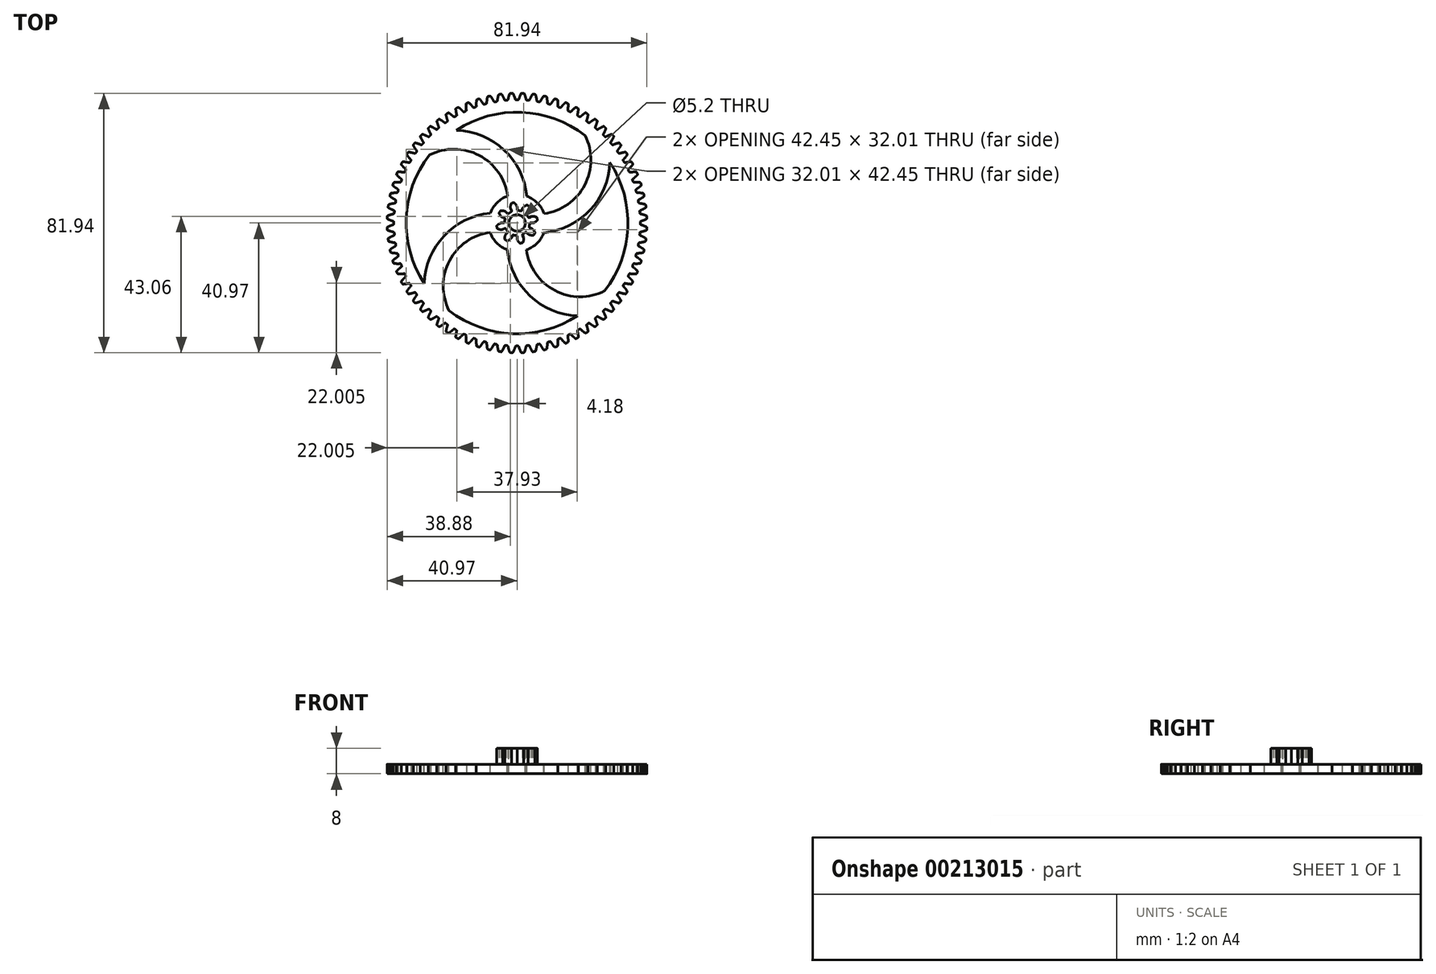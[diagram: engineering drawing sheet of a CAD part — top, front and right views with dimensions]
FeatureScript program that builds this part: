
annotation { "Feature Type Name" : "Feature", "Feature Type Description" : "" }
export const myFeature = defineFeature(function(context is Context, id is Id, definition is map)
    precondition{}
    {
        {
            var Q0;
            Q0=qCreatedBy(makeId("Top.planeOp"),FACE);
            var sketch = newSketch(context, id + "F0", { "sketchPlane" : qUnion([Q0])});
            skCircle(sketch, "E0", {"center": v(0, 0) * mm, "radius": 37.59 * mm, "construction": true});
            skLineSegment(sketch, "E1", {"start": v(37.59, 0) * mm, "end": v(37.59, 0) * mm});
            skLineSegment(sketch, "E2", {"start": v(0, 0) * mm, "end": v(37.55, 1.64) * mm, "construction": true});
            skLineSegment(sketch, "E3", {"start": v(37.55, 1.64) * mm, "end": v(37.62, 0) * mm, "construction": true});
            skLineSegment(sketch, "E4", {"start": v(0, 0) * mm, "end": v(37.44, 3.28) * mm, "construction": true});
            skLineSegment(sketch, "E5", {"start": v(37.44, 3.28) * mm, "end": v(37.73, 0) * mm, "construction": true});
            skLineSegment(sketch, "E6", {"start": v(0, 0) * mm, "end": v(37.27, 4.9) * mm, "construction": true});
            skLineSegment(sketch, "E7", {"start": v(37.27, 4.9) * mm, "end": v(37.9, 0.03) * mm, "construction": true});
            skLineSegment(sketch, "E8", {"start": v(0, 0) * mm, "end": v(37.02, 6.53) * mm, "construction": true});
            skLineSegment(sketch, "E9", {"start": v(37.02, 6.53) * mm, "end": v(38.16, 0.07) * mm, "construction": true});
            skLineSegment(sketch, "E10", {"start": v(0, 0) * mm, "end": v(36.7, 8.14) * mm, "construction": true});
            skLineSegment(sketch, "E11", {"start": v(36.7, 8.14) * mm, "end": v(38.47, 0.13) * mm, "construction": true});
            skLineSegment(sketch, "E12", {"start": v(0, 0) * mm, "end": v(36.3, 9.73) * mm, "construction": true});
            skLineSegment(sketch, "E13", {"start": v(36.3, 9.73) * mm, "end": v(38.85, 0.22) * mm, "construction": true});
            skLineSegment(sketch, "E14", {"start": v(0, 0) * mm, "end": v(35.85, 11.3) * mm, "construction": true});
            skLineSegment(sketch, "E15", {"start": v(35.85, 11.3) * mm, "end": v(39.3, 0.35) * mm, "construction": true});
            skLineSegment(sketch, "E16", {"start": v(0, 0) * mm, "end": v(35.32, 12.86) * mm, "construction": true});
            skLineSegment(sketch, "E17", {"start": v(35.32, 12.86) * mm, "end": v(39.8, 0.53) * mm, "construction": true});
            skLineSegment(sketch, "E18", {"start": v(0, 0) * mm, "end": v(34.73, 14.38) * mm, "construction": true});
            skLineSegment(sketch, "E19", {"start": v(34.73, 14.38) * mm, "end": v(40.38, 0.75) * mm, "construction": true});
            skLineSegment(sketch, "E20", {"start": v(0, 0) * mm, "end": v(34.07, 15.89) * mm, "construction": true});
            skLineSegment(sketch, "E21", {"start": v(34.07, 15.89) * mm, "end": v(41, 1.02) * mm, "construction": true});
            skPoint(sketch, "E22", {"position": v(37.59, 0) * mm});
            skCircle(sketch, "E23", {"center": v(0, 0) * mm, "radius": 38.89 * mm});
            skFitSpline(sketch, "E24", {"points": [v(37.59, 0) * mm, v(37.62, 0) * mm, v(37.73, 0) * mm, v(37.9, 0.03) * mm, v(38.16, 0.07) * mm, v(38.47, 0.13) * mm, v(38.85, 0.22) * mm, v(39.3, 0.35) * mm, v(39.8, 0.53) * mm, v(40.38, 0.75) * mm, v(41, 1.02) * mm], "startDerivative": vector(0.94, 0.02) * mm, "endDerivative": vector(4.3, 1.94) * mm, "construction": true});
            skPoint(sketch, "E25", {"position": v(40.99, 1.02) * mm});
            skPoint(sketch, "E26", {"position": v(38.89, 0.23) * mm});
            skFitSpline(sketch, "E27", {"points": [v(37.59, 0) * mm, v(37.62, 0) * mm, v(37.73, 0) * mm, v(37.9, 0.03) * mm, v(38.16, 0.07) * mm, v(38.47, 0.13) * mm, v(38.85, 0.22) * mm, v(39.3, 0.35) * mm, v(39.8, 0.53) * mm, v(40.38, 0.75) * mm, v(41, 1.02) * mm], "startDerivative": vector(0.94, 0.02) * mm, "endDerivative": vector(4.3, 1.94) * mm});
            skLineSegment(sketch, "E28", {"start": v(0, 0) * mm, "end": v(51.23, 1.88) * mm, "construction": true});
            skFitSpline(sketch, "E29.MirrorCS", {"points": [v(37.49, 2.76) * mm, v(37.52, 2.76) * mm, v(37.63, 2.76) * mm, v(37.8, 2.75) * mm, v(38.06, 2.73) * mm, v(38.38, 2.7) * mm, v(38.77, 2.63) * mm, v(39.22, 2.53) * mm, v(39.74, 2.4) * mm, v(40.32, 2.22) * mm, v(40.96, 1.99) * mm], "startDerivative": vector(0.93, 0.05) * mm, "endDerivative": vector(4.43, -1.62) * mm});
            skArc(sketch, "E30", {"start": v(40.95, 2) * mm, "mid": v(-40.97, -1.5) * mm, "end": v(40.99, 1.02) * mm, "construction": true});
            skArc(sketch, "E31", {"start": v(40.99, 1.02) * mm, "mid": v(40.97, 1.5) * mm, "end": v(40.95, 2) * mm});
            skSolve(sketch);
        }
        {
            var Q0;
            Q0=qCreatedBy(makeId("Front.planeOp"),FACE);
            var sketch = newSketch(context, id + "F1", { "sketchPlane" : qUnion([Q0])});
            skLineSegment(sketch, "E32", {"start": v(0, 0) * mm, "end": v(0, 57.42) * mm, "construction": true});
            skSolve(sketch);
        }
        {
            var Q0;
            {var subQ0=sQuery(id+"F0.wireOp",EDGE,"E23");var subQ1=makeQuery(id+"F0.imprint","INTERSECT",VERTEX,{"derivedFrom":[subQ0,sQuery(id+"F0.wireOp",EDGE,"E27")]});Q0=makeQuery(id+"F0.imprint","IMPRINT",FACE,{"disambiguationData":[TD([[makeQuery(id+"F0.imprint","IMPRINT",EDGE,{"disambiguationData":[TD([[subQ1,-1.0]])],"derivedFrom":subQ0}),1.0]])]});}
            var Q1;
            {var subQ0=sQuery(id+"F0.wireOp",EDGE,"E27");Q1=makeQuery(id+"F0.imprint","IMPRINT",FACE,{"disambiguationData":[TD([[makeQuery(id+"F0.imprint","IMPRINT",EDGE,{"derivedFrom":subQ0}),1.0]])]});}
            extrude(context, id + "F2", {"entities" : qUnion([Q0, Q1]), "depth" : 3 * mm});
        }
        {
            var Q0;
            Q0=makeQuery(id+"F2.opExtrude","SWEPT_EDGE",EDGE,{"disambiguationData":[OSD([sQuery(id+"F0.wireOp",EDGE,"E23"),sQuery(id+"F0.wireOp",EDGE,"E29.MirrorCS")])]});
            var Q1;
            Q1=makeQuery(id+"F2.opExtrude","SWEPT_EDGE",EDGE,{"disambiguationData":[OSD([sQuery(id+"F0.wireOp",EDGE,"E29.MirrorCS"),sQuery(id+"F0.wireOp",EDGE,"E31")])]});
            var Q2;
            Q2=makeQuery(id+"F2.opExtrude","SWEPT_EDGE",EDGE,{"disambiguationData":[OSD([sQuery(id+"F0.wireOp",EDGE,"E27"),sQuery(id+"F0.wireOp",EDGE,"E31")])]});
            var Q3;
            Q3=makeQuery(id+"F2.opExtrude","SWEPT_EDGE",EDGE,{"disambiguationData":[OSD([sQuery(id+"F0.wireOp",EDGE,"E23"),sQuery(id+"F0.wireOp",EDGE,"E27")])]});
            fillet(context, id + "F3", {"entities" : qUnion([Q0, Q1, Q2, Q3]), "radius" : 0.3 * mm, "tangentPropagation" : true, "allowEdgeOverflow" : false});
        }
        {
            var Q0;
            Q0=makeQuery(id+"F2.opExtrude","SWEPT_BODY",BODY,{"disambiguationData":[OSD([sQuery(id+"F0.wireOp",EDGE,"E23"),sQuery(id+"F0.wireOp",EDGE,"E27"),sQuery(id+"F0.wireOp",EDGE,"E29.MirrorCS"),sQuery(id+"F0.wireOp",EDGE,"E31")])]});
            var Q1;
            Q1=sQuery(id+"F1.wireOp",EDGE,"E32");
            circularPattern(context, id + "F4", {"operationType" : NewBodyOperationType.ADD, "entities" : qUnion([Q0]), "axis" : qUnion([Q1]), "angle" : 360 * degree, "instanceCount" : 72, "equalSpace" : true});
        }
        {
            var Q0;
            {var subQ0=makeQuery(id+"F2.opExtrude","CAP_FACE",FACE,{"disambiguationData":[OSD([sQuery(id+"F0.wireOp",EDGE,"E23"),sQuery(id+"F0.wireOp",EDGE,"E27"),sQuery(id+"F0.wireOp",EDGE,"E29.MirrorCS"),sQuery(id+"F0.wireOp",EDGE,"E31")])],"isStart":false});Q0=makeQuery(id+"F4.boolean.opBoolean","MERGE",FACE,{"derivedFrom":[subQ0,makeQuery(id+"F4.opPattern","COPY",FACE,{"derivedFrom":subQ0,"instanceName":"1"}),makeQuery(id+"F4.opPattern","COPY",FACE,{"derivedFrom":subQ0,"instanceName":"2"}),makeQuery(id+"F4.opPattern","COPY",FACE,{"derivedFrom":subQ0,"instanceName":"3"}),makeQuery(id+"F4.opPattern","COPY",FACE,{"derivedFrom":subQ0,"instanceName":"4"}),makeQuery(id+"F4.opPattern","COPY",FACE,{"derivedFrom":subQ0,"instanceName":"5"}),makeQuery(id+"F4.opPattern","COPY",FACE,{"derivedFrom":subQ0,"instanceName":"6"}),makeQuery(id+"F4.opPattern","COPY",FACE,{"derivedFrom":subQ0,"instanceName":"7"}),makeQuery(id+"F4.opPattern","COPY",FACE,{"derivedFrom":subQ0,"instanceName":"8"}),makeQuery(id+"F4.opPattern","COPY",FACE,{"derivedFrom":subQ0,"instanceName":"9"}),makeQuery(id+"F4.opPattern","COPY",FACE,{"derivedFrom":subQ0,"instanceName":"10"}),makeQuery(id+"F4.opPattern","COPY",FACE,{"derivedFrom":subQ0,"instanceName":"11"}),makeQuery(id+"F4.opPattern","COPY",FACE,{"derivedFrom":subQ0,"instanceName":"12"}),makeQuery(id+"F4.opPattern","COPY",FACE,{"derivedFrom":subQ0,"instanceName":"13"}),makeQuery(id+"F4.opPattern","COPY",FACE,{"derivedFrom":subQ0,"instanceName":"14"}),makeQuery(id+"F4.opPattern","COPY",FACE,{"derivedFrom":subQ0,"instanceName":"15"}),makeQuery(id+"F4.opPattern","COPY",FACE,{"derivedFrom":subQ0,"instanceName":"16"}),makeQuery(id+"F4.opPattern","COPY",FACE,{"derivedFrom":subQ0,"instanceName":"17"}),makeQuery(id+"F4.opPattern","COPY",FACE,{"derivedFrom":subQ0,"instanceName":"18"}),makeQuery(id+"F4.opPattern","COPY",FACE,{"derivedFrom":subQ0,"instanceName":"19"}),makeQuery(id+"F4.opPattern","COPY",FACE,{"derivedFrom":subQ0,"instanceName":"20"}),makeQuery(id+"F4.opPattern","COPY",FACE,{"derivedFrom":subQ0,"instanceName":"21"}),makeQuery(id+"F4.opPattern","COPY",FACE,{"derivedFrom":subQ0,"instanceName":"22"}),makeQuery(id+"F4.opPattern","COPY",FACE,{"derivedFrom":subQ0,"instanceName":"23"}),makeQuery(id+"F4.opPattern","COPY",FACE,{"derivedFrom":subQ0,"instanceName":"24"}),makeQuery(id+"F4.opPattern","COPY",FACE,{"derivedFrom":subQ0,"instanceName":"25"}),makeQuery(id+"F4.opPattern","COPY",FACE,{"derivedFrom":subQ0,"instanceName":"26"}),makeQuery(id+"F4.opPattern","COPY",FACE,{"derivedFrom":subQ0,"instanceName":"27"}),makeQuery(id+"F4.opPattern","COPY",FACE,{"derivedFrom":subQ0,"instanceName":"28"}),makeQuery(id+"F4.opPattern","COPY",FACE,{"derivedFrom":subQ0,"instanceName":"29"}),makeQuery(id+"F4.opPattern","COPY",FACE,{"derivedFrom":subQ0,"instanceName":"30"}),makeQuery(id+"F4.opPattern","COPY",FACE,{"derivedFrom":subQ0,"instanceName":"31"}),makeQuery(id+"F4.opPattern","COPY",FACE,{"derivedFrom":subQ0,"instanceName":"32"}),makeQuery(id+"F4.opPattern","COPY",FACE,{"derivedFrom":subQ0,"instanceName":"33"}),makeQuery(id+"F4.opPattern","COPY",FACE,{"derivedFrom":subQ0,"instanceName":"34"}),makeQuery(id+"F4.opPattern","COPY",FACE,{"derivedFrom":subQ0,"instanceName":"35"}),makeQuery(id+"F4.opPattern","COPY",FACE,{"derivedFrom":subQ0,"instanceName":"36"}),makeQuery(id+"F4.opPattern","COPY",FACE,{"derivedFrom":subQ0,"instanceName":"37"}),makeQuery(id+"F4.opPattern","COPY",FACE,{"derivedFrom":subQ0,"instanceName":"38"}),makeQuery(id+"F4.opPattern","COPY",FACE,{"derivedFrom":subQ0,"instanceName":"39"}),makeQuery(id+"F4.opPattern","COPY",FACE,{"derivedFrom":subQ0,"instanceName":"40"}),makeQuery(id+"F4.opPattern","COPY",FACE,{"derivedFrom":subQ0,"instanceName":"41"}),makeQuery(id+"F4.opPattern","COPY",FACE,{"derivedFrom":subQ0,"instanceName":"42"}),makeQuery(id+"F4.opPattern","COPY",FACE,{"derivedFrom":subQ0,"instanceName":"43"}),makeQuery(id+"F4.opPattern","COPY",FACE,{"derivedFrom":subQ0,"instanceName":"44"}),makeQuery(id+"F4.opPattern","COPY",FACE,{"derivedFrom":subQ0,"instanceName":"45"}),makeQuery(id+"F4.opPattern","COPY",FACE,{"derivedFrom":subQ0,"instanceName":"46"}),makeQuery(id+"F4.opPattern","COPY",FACE,{"derivedFrom":subQ0,"instanceName":"47"}),makeQuery(id+"F4.opPattern","COPY",FACE,{"derivedFrom":subQ0,"instanceName":"48"}),makeQuery(id+"F4.opPattern","COPY",FACE,{"derivedFrom":subQ0,"instanceName":"49"}),makeQuery(id+"F4.opPattern","COPY",FACE,{"derivedFrom":subQ0,"instanceName":"50"}),makeQuery(id+"F4.opPattern","COPY",FACE,{"derivedFrom":subQ0,"instanceName":"51"}),makeQuery(id+"F4.opPattern","COPY",FACE,{"derivedFrom":subQ0,"instanceName":"52"}),makeQuery(id+"F4.opPattern","COPY",FACE,{"derivedFrom":subQ0,"instanceName":"53"}),makeQuery(id+"F4.opPattern","COPY",FACE,{"derivedFrom":subQ0,"instanceName":"54"}),makeQuery(id+"F4.opPattern","COPY",FACE,{"derivedFrom":subQ0,"instanceName":"55"}),makeQuery(id+"F4.opPattern","COPY",FACE,{"derivedFrom":subQ0,"instanceName":"56"}),makeQuery(id+"F4.opPattern","COPY",FACE,{"derivedFrom":subQ0,"instanceName":"57"}),makeQuery(id+"F4.opPattern","COPY",FACE,{"derivedFrom":subQ0,"instanceName":"58"}),makeQuery(id+"F4.opPattern","COPY",FACE,{"derivedFrom":subQ0,"instanceName":"59"}),makeQuery(id+"F4.opPattern","COPY",FACE,{"derivedFrom":subQ0,"instanceName":"60"}),makeQuery(id+"F4.opPattern","COPY",FACE,{"derivedFrom":subQ0,"instanceName":"61"}),makeQuery(id+"F4.opPattern","COPY",FACE,{"derivedFrom":subQ0,"instanceName":"62"}),makeQuery(id+"F4.opPattern","COPY",FACE,{"derivedFrom":subQ0,"instanceName":"63"}),makeQuery(id+"F4.opPattern","COPY",FACE,{"derivedFrom":subQ0,"instanceName":"64"}),makeQuery(id+"F4.opPattern","COPY",FACE,{"derivedFrom":subQ0,"instanceName":"65"}),makeQuery(id+"F4.opPattern","COPY",FACE,{"derivedFrom":subQ0,"instanceName":"66"}),makeQuery(id+"F4.opPattern","COPY",FACE,{"derivedFrom":subQ0,"instanceName":"67"}),makeQuery(id+"F4.opPattern","COPY",FACE,{"derivedFrom":subQ0,"instanceName":"68"}),makeQuery(id+"F4.opPattern","COPY",FACE,{"derivedFrom":subQ0,"instanceName":"69"}),makeQuery(id+"F4.opPattern","COPY",FACE,{"derivedFrom":subQ0,"instanceName":"70"}),makeQuery(id+"F4.opPattern","COPY",FACE,{"derivedFrom":subQ0,"instanceName":"71"})]});}
            var sketch = newSketch(context, id + "F5", { "sketchPlane" : qUnion([Q0])});
            skLineSegment(sketch, "E33", {"start": v(38.93, -0.27) * mm, "end": v(0, 0) * mm, "construction": true});
            skPoint(sketch, "E33.startSnap0", {"position": v(38.89, -0.27) * mm});
            skCircle(sketch, "E34", {"center": v(0, 0) * mm, "radius": 4.97 * mm, "construction": true});
            skLineSegment(sketch, "E35", {"start": v(-2.75, -4.33) * mm, "end": v(-2.75, -4.33) * mm});
            skLineSegment(sketch, "E36", {"start": v(0, 0) * mm, "end": v(4.96, 0.42) * mm, "construction": true});
            skLineSegment(sketch, "E37", {"start": v(4.96, 0.42) * mm, "end": v(5, 0) * mm, "construction": true});
            skLineSegment(sketch, "E38", {"start": v(0, 0) * mm, "end": v(4.9, 0.85) * mm, "construction": true});
            skLineSegment(sketch, "E39", {"start": v(4.9, 0.85) * mm, "end": v(5.05, 0) * mm, "construction": true});
            skLineSegment(sketch, "E40", {"start": v(0, 0) * mm, "end": v(4.81, 1.26) * mm, "construction": true});
            skLineSegment(sketch, "E41", {"start": v(4.81, 1.26) * mm, "end": v(5.14, 0.03) * mm, "construction": true});
            skLineSegment(sketch, "E42", {"start": v(0, 0) * mm, "end": v(4.69, 1.67) * mm, "construction": true});
            skLineSegment(sketch, "E43", {"start": v(4.69, 1.67) * mm, "end": v(5.26, 0.07) * mm, "construction": true});
            skLineSegment(sketch, "E44", {"start": v(0, 0) * mm, "end": v(4.53, 2.06) * mm, "construction": true});
            skLineSegment(sketch, "E45", {"start": v(4.53, 2.06) * mm, "end": v(5.4, 0.13) * mm, "construction": true});
            skLineSegment(sketch, "E46", {"start": v(0, 0) * mm, "end": v(4.33, 2.44) * mm, "construction": true});
            skLineSegment(sketch, "E47", {"start": v(4.33, 2.44) * mm, "end": v(5.59, 0.22) * mm, "construction": true});
            skLineSegment(sketch, "E48", {"start": v(0, 0) * mm, "end": v(4.1, 2.8) * mm, "construction": true});
            skLineSegment(sketch, "E49", {"start": v(4.1, 2.8) * mm, "end": v(5.79, 0.34) * mm, "construction": true});
            skLineSegment(sketch, "E50", {"start": v(0, 0) * mm, "end": v(3.86, 3.14) * mm, "construction": true});
            skLineSegment(sketch, "E51", {"start": v(3.86, 3.14) * mm, "end": v(6, 0.5) * mm, "construction": true});
            skLineSegment(sketch, "E52", {"start": v(0, 0) * mm, "end": v(3.57, 3.46) * mm, "construction": true});
            skLineSegment(sketch, "E53", {"start": v(3.57, 3.46) * mm, "end": v(6.24, 0.71) * mm, "construction": true});
            skLineSegment(sketch, "E54", {"start": v(0, 0) * mm, "end": v(3.26, 3.75) * mm, "construction": true});
            skLineSegment(sketch, "E55", {"start": v(3.26, 3.75) * mm, "end": v(6.47, 0.96) * mm, "construction": true});
            skPoint(sketch, "E56", {"position": v(4.97, 0) * mm});
            skCircle(sketch, "E57", {"center": v(0, 0) * mm, "radius": 3.97 * mm});
            skLineSegment(sketch, "E58", {"start": v(3.97, 0) * mm, "end": v(4.97, 0) * mm});
            skFitSpline(sketch, "E59", {"points": [v(4.97, 0) * mm, v(5, 0) * mm, v(5.05, 0) * mm, v(5.14, 0.03) * mm, v(5.26, 0.07) * mm, v(5.4, 0.13) * mm, v(5.59, 0.22) * mm, v(5.79, 0.34) * mm, v(6, 0.5) * mm, v(6.24, 0.71) * mm, v(6.47, 0.96) * mm], "startDerivative": vector(0.48, 0.02) * mm, "endDerivative": vector(1.62, 1.77) * mm});
            skFitSpline(sketch, "E60", {"points": [v(4.97, 0) * mm, v(5, 0) * mm, v(5.05, 0) * mm, v(5.14, 0.03) * mm, v(5.26, 0.07) * mm, v(5.4, 0.13) * mm, v(5.59, 0.22) * mm, v(5.79, 0.34) * mm, v(6, 0.5) * mm, v(6.24, 0.71) * mm, v(6.47, 0.96) * mm], "startDerivative": vector(0.48, 0.02) * mm, "endDerivative": vector(1.62, 1.77) * mm, "construction": true});
            skLineSegment(sketch, "E61", {"start": v(0, 0) * mm, "end": v(9.9, 2.12) * mm, "construction": true});
            skLineSegment(sketch, "E62.MirrorCS", {"start": v(3.62, 1.63) * mm, "end": v(4.54, 2.04) * mm});
            skFitSpline(sketch, "E63.MirrorCS", {"points": [v(4.54, 2.04) * mm, v(4.55, 2.05) * mm, v(4.6, 2.06) * mm, v(4.7, 2.08) * mm, v(4.82, 2.1) * mm, v(4.99, 2.1) * mm, v(5.19, 2.1) * mm, v(5.42, 2.06) * mm, v(5.69, 2) * mm, v(5.98, 1.9) * mm, v(6.3, 1.78) * mm], "startDerivative": vector(0.44, 0.18) * mm, "endDerivative": vector(2.2, -0.95) * mm});
            skArc(sketch, "E64", {"start": v(6.23, 1.8) * mm, "mid": v(-6.34, -1.36) * mm, "end": v(6.42, 0.9) * mm, "construction": true});
            skArc(sketch, "E65", {"start": v(6.42, 0.9) * mm, "mid": v(6.34, 1.36) * mm, "end": v(6.23, 1.8) * mm});
            skSolve(sketch);
        }
        {
            var Q0;
            Q0=makeQuery(id+"F2.opExtrude","SWEPT_BODY",BODY,{"disambiguationData":[OSD([sQuery(id+"F0.wireOp",EDGE,"E23"),sQuery(id+"F0.wireOp",EDGE,"E27"),sQuery(id+"F0.wireOp",EDGE,"E29.MirrorCS"),sQuery(id+"F0.wireOp",EDGE,"E31")])]});
            var Q1;
            Q1=sQuery(id+"F1.wireOp",EDGE,"E32");
            transform(context, id + "F6", {"entities" : qUnion([Q0]), "transformType" : TransformType.ROTATION, "transformAxis" : qUnion([Q1]), "angle" : 0.4 * degree, "makeCopy" : false});
        }
        {
            var Q0;
            {var subQ0=sQuery(id+"F5.wireOp",EDGE,"E57");var subQ1=makeQuery(id+"F5.imprint","INTERSECT",VERTEX,{"derivedFrom":[subQ0,sQuery(id+"F5.wireOp",EDGE,"E58")]});Q0=makeQuery(id+"F5.imprint","IMPRINT",FACE,{"disambiguationData":[TD([[makeQuery(id+"F5.imprint","IMPRINT",EDGE,{"disambiguationData":[TD([[subQ1,-1.0]])],"derivedFrom":subQ0}),1.0]])]});}
            var Q1;
            {var subQ1=sQuery(id+"F5.wireOp",EDGE,"E58");Q1=makeQuery(id+"F5.imprint","IMPRINT",FACE,{"disambiguationData":[TD([[makeQuery(id+"F5.imprint","IMPRINT",EDGE,{"derivedFrom":subQ1}),1.0]])]});}
            extrude(context, id + "F7", {"entities" : qUnion([Q0, Q1]), "depth" : 5 * mm});
        }
        {
            var Q0;
            Q0=makeQuery(id+"F7.opExtrude","SWEPT_EDGE",EDGE,{"disambiguationData":[OSD([sQuery(id+"F5.wireOp",EDGE,"E57"),sQuery(id+"F5.wireOp",EDGE,"E58")])]});
            var Q1;
            Q1=makeQuery(id+"F7.opExtrude","SWEPT_EDGE",EDGE,{"disambiguationData":[OSD([sQuery(id+"F5.wireOp",EDGE,"E59"),sQuery(id+"F5.wireOp",EDGE,"E65")])]});
            var Q2;
            Q2=makeQuery(id+"F7.opExtrude","SWEPT_EDGE",EDGE,{"disambiguationData":[OSD([sQuery(id+"F5.wireOp",EDGE,"E63.MirrorCS"),sQuery(id+"F5.wireOp",EDGE,"E65")])]});
            var Q3;
            Q3=makeQuery(id+"F7.opExtrude","SWEPT_EDGE",EDGE,{"disambiguationData":[OSD([sQuery(id+"F5.wireOp",EDGE,"E57"),sQuery(id+"F5.wireOp",EDGE,"E62.MirrorCS")])]});
            fillet(context, id + "F8", {"entities" : qUnion([Q0, Q1, Q2, Q3]), "radius" : 0.3 * mm, "tangentPropagation" : true, "allowEdgeOverflow" : false});
        }
        {
            var Q0;
            Q0=makeQuery(id+"F7.opExtrude","SWEPT_BODY",BODY,{"disambiguationData":[OSD([sQuery(id+"F5.wireOp",EDGE,"E57"),sQuery(id+"F5.wireOp",EDGE,"E58"),sQuery(id+"F5.wireOp",EDGE,"E59"),sQuery(id+"F5.wireOp",EDGE,"E62.MirrorCS"),sQuery(id+"F5.wireOp",EDGE,"E63.MirrorCS"),sQuery(id+"F5.wireOp",EDGE,"E65")])]});
            var Q1;
            Q1=sQuery(id+"F1.wireOp",EDGE,"E32");
            circularPattern(context, id + "F9", {"operationType" : NewBodyOperationType.ADD, "entities" : qUnion([Q0]), "axis" : qUnion([Q1]), "angle" : 360 * degree, "instanceCount" : 8, "equalSpace" : true});
        }
        {
            var Q0;
            {var subQ0=makeQuery(id+"F7.opExtrude","CAP_FACE",FACE,{"disambiguationData":[OSD([sQuery(id+"F5.wireOp",EDGE,"E57"),sQuery(id+"F5.wireOp",EDGE,"E58"),sQuery(id+"F5.wireOp",EDGE,"E59"),sQuery(id+"F5.wireOp",EDGE,"E62.MirrorCS"),sQuery(id+"F5.wireOp",EDGE,"E63.MirrorCS"),sQuery(id+"F5.wireOp",EDGE,"E65")])],"isStart":false});Q0=makeQuery(id+"F9.boolean.opBoolean","MERGE",FACE,{"derivedFrom":[subQ0,makeQuery(id+"F9.opPattern","COPY",FACE,{"derivedFrom":subQ0,"instanceName":"1"}),makeQuery(id+"F9.opPattern","COPY",FACE,{"derivedFrom":subQ0,"instanceName":"2"}),makeQuery(id+"F9.opPattern","COPY",FACE,{"derivedFrom":subQ0,"instanceName":"3"}),makeQuery(id+"F9.opPattern","COPY",FACE,{"derivedFrom":subQ0,"instanceName":"4"}),makeQuery(id+"F9.opPattern","COPY",FACE,{"derivedFrom":subQ0,"instanceName":"5"}),makeQuery(id+"F9.opPattern","COPY",FACE,{"derivedFrom":subQ0,"instanceName":"6"}),makeQuery(id+"F9.opPattern","COPY",FACE,{"derivedFrom":subQ0,"instanceName":"7"})]});}
            var sketch = newSketch(context, id + "F10", { "sketchPlane" : qUnion([Q0])});
            skCircle(sketch, "E66", {"center": v(0, 0) * mm, "radius": 2.6 * mm});
            skSolve(sketch);
        }
        {
            var Q0;
            Q0=makeQuery(id+"F10.imprint","IMPRINT",FACE,{"disambiguationData":[TD([[makeQuery(id+"F10.imprint","IMPRINT",EDGE,{"derivedFrom":sQuery(id+"F10.wireOp",EDGE,"E66")}),1.0]])]});
            extrude(context, id + "F11", {"entities" : qUnion([Q0]), "operationType" : NewBodyOperationType.REMOVE, "endBound" : BoundingType.UP_TO_NEXT, "oppositeDirection" : true, "depth" : 25 * mm});
        }
        {
            var Q0;
            {var subQ6=sQuery(id+"F5.wireOp",EDGE,"E58");Q0=makeQuery(id+"F5.imprint","IMPRINT",FACE,{"disambiguationData":[TD([[makeQuery(id+"F5.imprint","IMPRINT",EDGE,{"derivedFrom":subQ6}),-1.0]])]});}
            var sketch = newSketch(context, id + "F12", { "sketchPlane" : qUnion([Q0])});
            skCircle(sketch, "E67", {"center": v(0, 0) * mm, "radius": 9 * mm});
            skCircle(sketch, "E68", {"center": v(0, 0) * mm, "radius": 35 * mm});
            skLineSegment(sketch, "E69", {"start": v(0, 0) * mm, "end": v(-23.42, 26.01) * mm, "construction": true});
            skCircle(sketch, "E70", {"center": v(-19.91, 6.2) * mm, "radius": 20.1 * mm, "construction": true});
            skPoint(sketch, "E70.first.point", {"position": v(0, 9) * mm});
            skPoint(sketch, "E70.third.point", {"position": v(-8.34, 22.65) * mm});
            skArc(sketch, "E71", {"start": v(3.09, 8.45) * mm, "mid": v(-4.1, 23.06) * mm, "end": v(-19.14, 29.3) * mm});
            skArc(sketch, "E72", {"start": v(-2.96, 8.5) * mm, "mid": v(-11.95, 21.35) * mm, "end": v(-27.64, 21.48) * mm});
            skArc(sketch, "E73.1.0", {"start": v(-8.5, -2.96) * mm, "mid": v(-21.35, -11.95) * mm, "end": v(-21.48, -27.64) * mm});
            skArc(sketch, "E73.1.1", {"start": v(-8.45, 3.09) * mm, "mid": v(-23.06, -4.1) * mm, "end": v(-29.3, -19.14) * mm});
            skArc(sketch, "E73.2.0", {"start": v(2.96, -8.5) * mm, "mid": v(11.95, -21.35) * mm, "end": v(27.64, -21.48) * mm});
            skArc(sketch, "E73.2.1", {"start": v(-3.09, -8.45) * mm, "mid": v(4.1, -23.06) * mm, "end": v(19.14, -29.3) * mm});
            skArc(sketch, "E73.3.0", {"start": v(8.5, 2.96) * mm, "mid": v(21.35, 11.95) * mm, "end": v(21.48, 27.64) * mm});
            skArc(sketch, "E73.3.1", {"start": v(8.45, -3.09) * mm, "mid": v(23.06, 4.1) * mm, "end": v(29.3, 19.14) * mm});
            skSolve(sketch);
        }
        {
            var Q0;
            {var subQ0=sQuery(id+"F12.wireOp",EDGE,"E72");Q0=makeQuery(id+"F12.imprint","IMPRINT",FACE,{"disambiguationData":[TD([[makeQuery(id+"F12.imprint","IMPRINT",EDGE,{"derivedFrom":subQ0}),1.0]])]});}
            var Q1;
            {var subQ0=sQuery(id+"F12.wireOp",EDGE,"E71");Q1=makeQuery(id+"F12.imprint","IMPRINT",FACE,{"disambiguationData":[TD([[makeQuery(id+"F12.imprint","IMPRINT",EDGE,{"derivedFrom":subQ0}),-1.0]])]});}
            var Q2;
            {var subQ0=sQuery(id+"F12.wireOp",EDGE,"E73.2.0");Q2=makeQuery(id+"F12.imprint","IMPRINT",FACE,{"disambiguationData":[TD([[makeQuery(id+"F12.imprint","IMPRINT",EDGE,{"derivedFrom":subQ0}),1.0]])]});}
            var Q3;
            {var subQ0=sQuery(id+"F12.wireOp",EDGE,"E73.1.0");Q3=makeQuery(id+"F12.imprint","IMPRINT",FACE,{"disambiguationData":[TD([[makeQuery(id+"F12.imprint","IMPRINT",EDGE,{"derivedFrom":subQ0}),1.0]])]});}
            extrude(context, id + "F13", {"entities" : qUnion([Q0, Q1, Q2, Q3]), "operationType" : NewBodyOperationType.REMOVE, "endBound" : BoundingType.UP_TO_NEXT, "oppositeDirection" : true, "depth" : 25 * mm});
        }
    });
